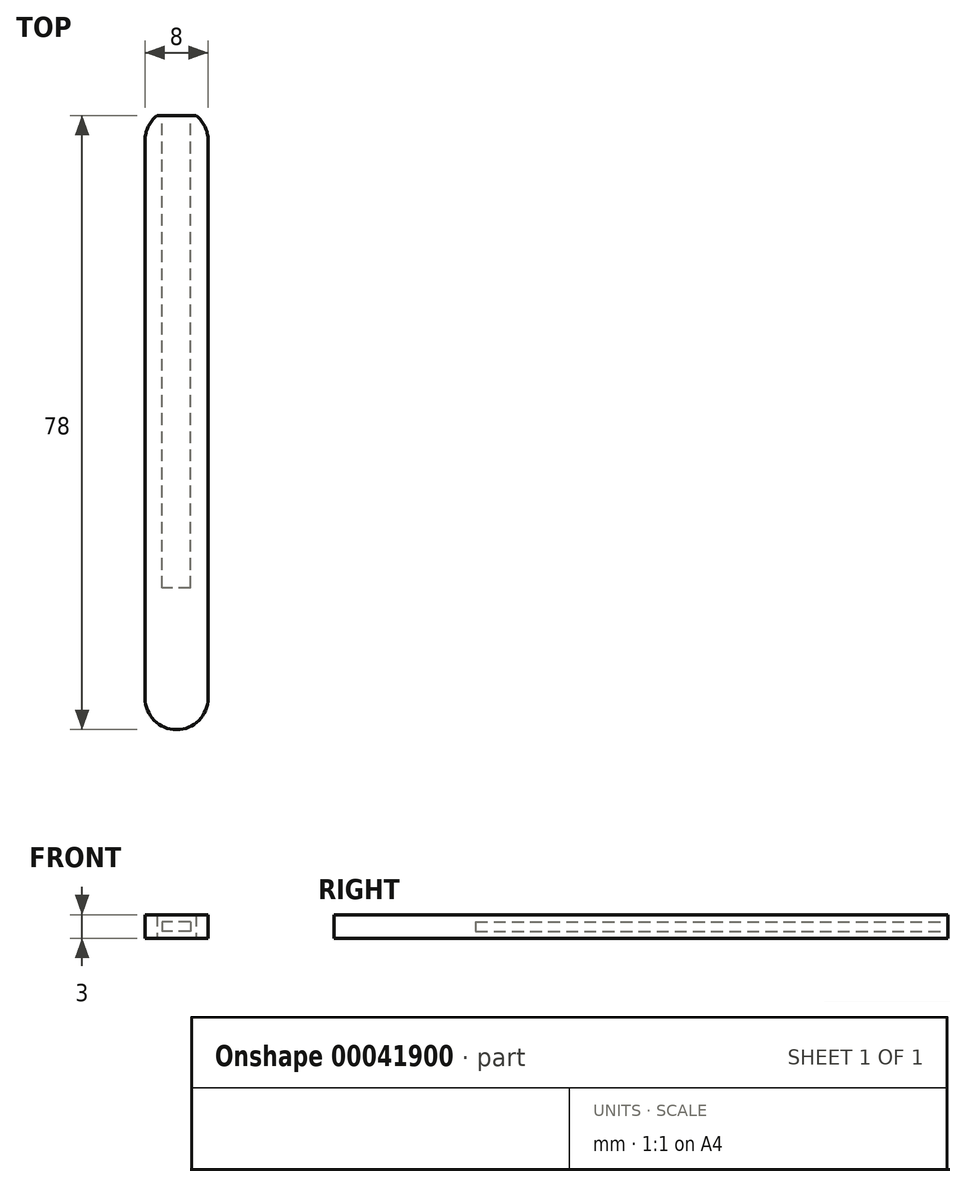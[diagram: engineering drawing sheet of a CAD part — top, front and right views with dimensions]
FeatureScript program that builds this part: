
annotation { "Feature Type Name" : "Feature", "Feature Type Description" : "" }
export const myFeature = defineFeature(function(context is Context, id is Id, definition is map)
    precondition{}
    {
        {
            var Q0;
            Q0=qCreatedBy(makeId("Top.planeOp"),FACE);
            var sketch = newSketch(context, id + "F0", { "sketchPlane" : qUnion([Q0])});
            skArc(sketch, "E0", {"start": v(4.02, 0) * mm, "mid": v(3.63, 1.73) * mm, "end": v(2.52, 3.12) * mm});
            skLineSegment(sketch, "E1", {"start": v(-3.98, 0) * mm, "end": v(-3.98, -70.88) * mm});
            skArc(sketch, "E2", {"start": v(-3.98, -70.88) * mm, "mid": v(0.02, -74.88) * mm, "end": v(4.02, -70.88) * mm});
            skLineSegment(sketch, "E3", {"start": v(4.02, 0) * mm, "end": v(4.02, -70.88) * mm});
            skLineSegment(sketch, "E4", {"start": v(-2.48, 3.12) * mm, "end": v(2.52, 3.12) * mm});
            skArc(sketch, "E5.trimOffspring", {"start": v(-2.48, 3.12) * mm, "mid": v(-3.58, 1.73) * mm, "end": v(-3.98, 0) * mm});
            skPoint(sketch, "E6", {"position": v(0, -74.88) * mm});
            skSolve(sketch);
        }
        {
            var Q0;
            Q0=makeQuery(id+"F0.imprint","IMPRINT",FACE,{"disambiguationData":[TD([[makeQuery(id+"F0.imprint","IMPRINT",EDGE,{"derivedFrom":sQuery(id+"F0.wireOp",EDGE,"E0")}),1.0]])]});
            extrude(context, id + "F1", {"entities" : qUnion([Q0]), "depth" : 3 * mm});
        }
        {
            var Q0;
            Q0=makeQuery(id+"F1.opExtrude","SWEPT_FACE",FACE,{"disambiguationData":[OSD([sQuery(id+"F0.wireOp",EDGE,"E4")])]});
            var sketch = newSketch(context, id + "F2", { "sketchPlane" : qUnion([Q0])});
            skLineSegment(sketch, "E7.bottom", {"start": v(-1.8, 2.1) * mm, "end": v(1.8, 2.1) * mm});
            skLineSegment(sketch, "E7.top", {"start": v(-1.8, 0.9) * mm, "end": v(1.8, 0.9) * mm});
            skLineSegment(sketch, "E7.left", {"start": v(-1.8, 2.1) * mm, "end": v(-1.8, 0.9) * mm});
            skLineSegment(sketch, "E7.right", {"start": v(1.8, 2.1) * mm, "end": v(1.8, 0.9) * mm});
            skLineSegment(sketch, "E8", {"start": v(-1.8, 1.5) * mm, "end": v(-2.52, 1.5) * mm, "construction": true});
            skLineSegment(sketch, "E9", {"start": v(0, 2.1) * mm, "end": v(0, 3) * mm, "construction": true});
            skSolve(sketch);
        }
        {
            var Q0;
            Q0 = qSketchRegion(id + "F2", true);
            extrude(context, id + "F3", {"entities" : qUnion([Q0]), "operationType" : NewBodyOperationType.REMOVE, "oppositeDirection" : true, "depth" : 60 * mm});
        }
    });
